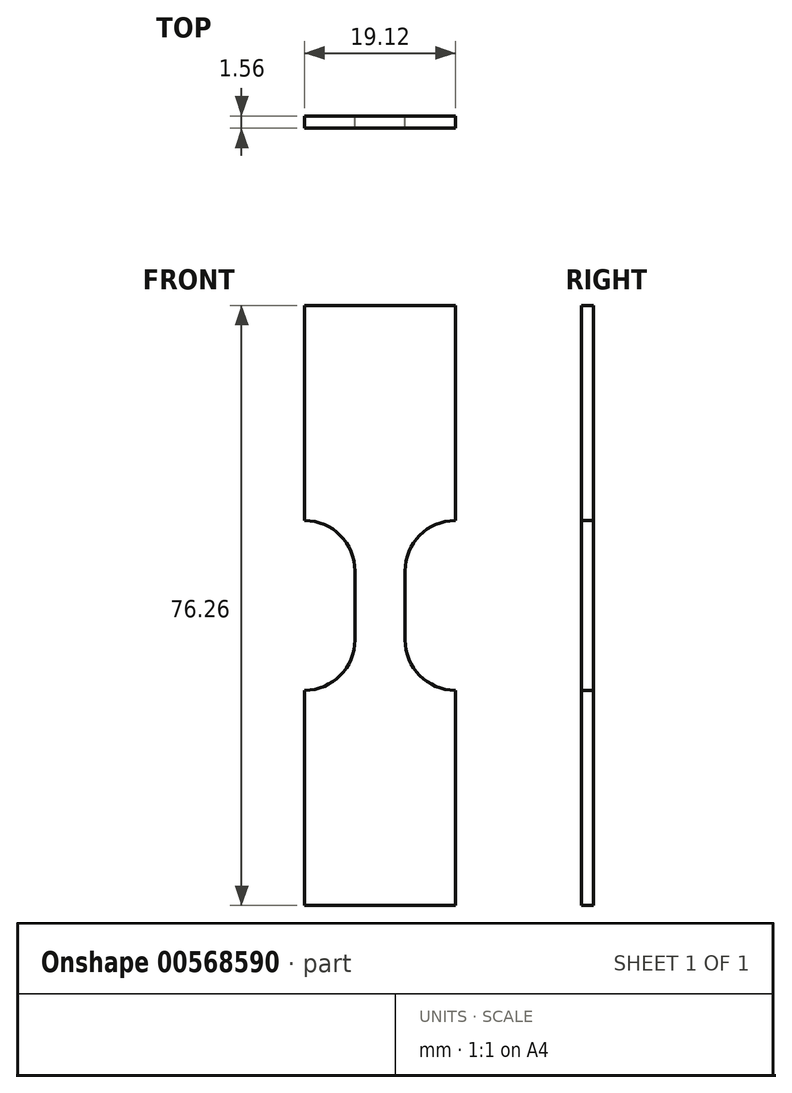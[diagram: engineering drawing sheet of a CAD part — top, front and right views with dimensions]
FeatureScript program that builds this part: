
annotation { "Feature Type Name" : "Feature", "Feature Type Description" : "" }
export const myFeature = defineFeature(function(context is Context, id is Id, definition is map)
    precondition{}
    {
        {
            var Q0;
            Q0=qCreatedBy(makeId("Front.planeOp"),FACE);
            var sketch = newSketch(context, id + "F0", { "sketchPlane" : qUnion([Q0])});
            skLineSegment(sketch, "E0", {"start": v(3.18, 0) * mm, "end": v(3.18, 4.39) * mm});
            skLineSegment(sketch, "E1", {"start": v(-3.18, 0) * mm, "end": v(-3.18, 4.39) * mm});
            skArc(sketch, "E2", {"start": v(-3.18, 4.39) * mm, "mid": v(-5.05, 8.9) * mm, "end": v(-9.56, 10.77) * mm});
            skArc(sketch, "E3", {"start": v(9.56, 10.77) * mm, "mid": v(5.05, 8.9) * mm, "end": v(3.18, 4.39) * mm});
            skLineSegment(sketch, "E4", {"start": v(-9.56, 10.77) * mm, "end": v(-9.56, 38.13) * mm});
            skLineSegment(sketch, "E5", {"start": v(9.56, 10.77) * mm, "end": v(9.56, 38.13) * mm});
            skLineSegment(sketch, "E6", {"start": v(-9.56, 38.13) * mm, "end": v(9.56, 38.13) * mm});
            skLineSegment(sketch, "E7.MirrorCS", {"start": v(-9.56, -38.13) * mm, "end": v(9.56, -38.13) * mm});
            skLineSegment(sketch, "E8.MirrorCS", {"start": v(9.56, -10.77) * mm, "end": v(9.56, -38.13) * mm});
            skLineSegment(sketch, "E9.MirrorCS", {"start": v(-9.56, -10.77) * mm, "end": v(-9.56, -38.13) * mm});
            skArc(sketch, "E10.MirrorCS", {"start": v(-3.18, -4.39) * mm, "mid": v(-5.05, -8.9) * mm, "end": v(-9.56, -10.77) * mm});
            skLineSegment(sketch, "E11.MirrorCS", {"start": v(-3.18, 0) * mm, "end": v(-3.18, -4.39) * mm});
            skLineSegment(sketch, "E12.MirrorCS", {"start": v(3.18, 0) * mm, "end": v(3.18, -4.39) * mm});
            skArc(sketch, "E13.MirrorCS", {"start": v(9.56, -10.77) * mm, "mid": v(5.05, -8.9) * mm, "end": v(3.18, -4.39) * mm});
            skSolve(sketch);
        }
        {
            var Q0;
            Q0=makeQuery(id+"F0.imprint","IMPRINT",FACE,{"disambiguationData":[TD([[makeQuery(id+"F0.imprint","IMPRINT",EDGE,{"derivedFrom":sQuery(id+"F0.wireOp",EDGE,"E0")}),1.0]])]});
            extrude(context, id + "F1", {"entities" : qUnion([Q0]), "depth" : 1.56 * mm, "offsetDistance" : 25 * mm});
        }
    });
